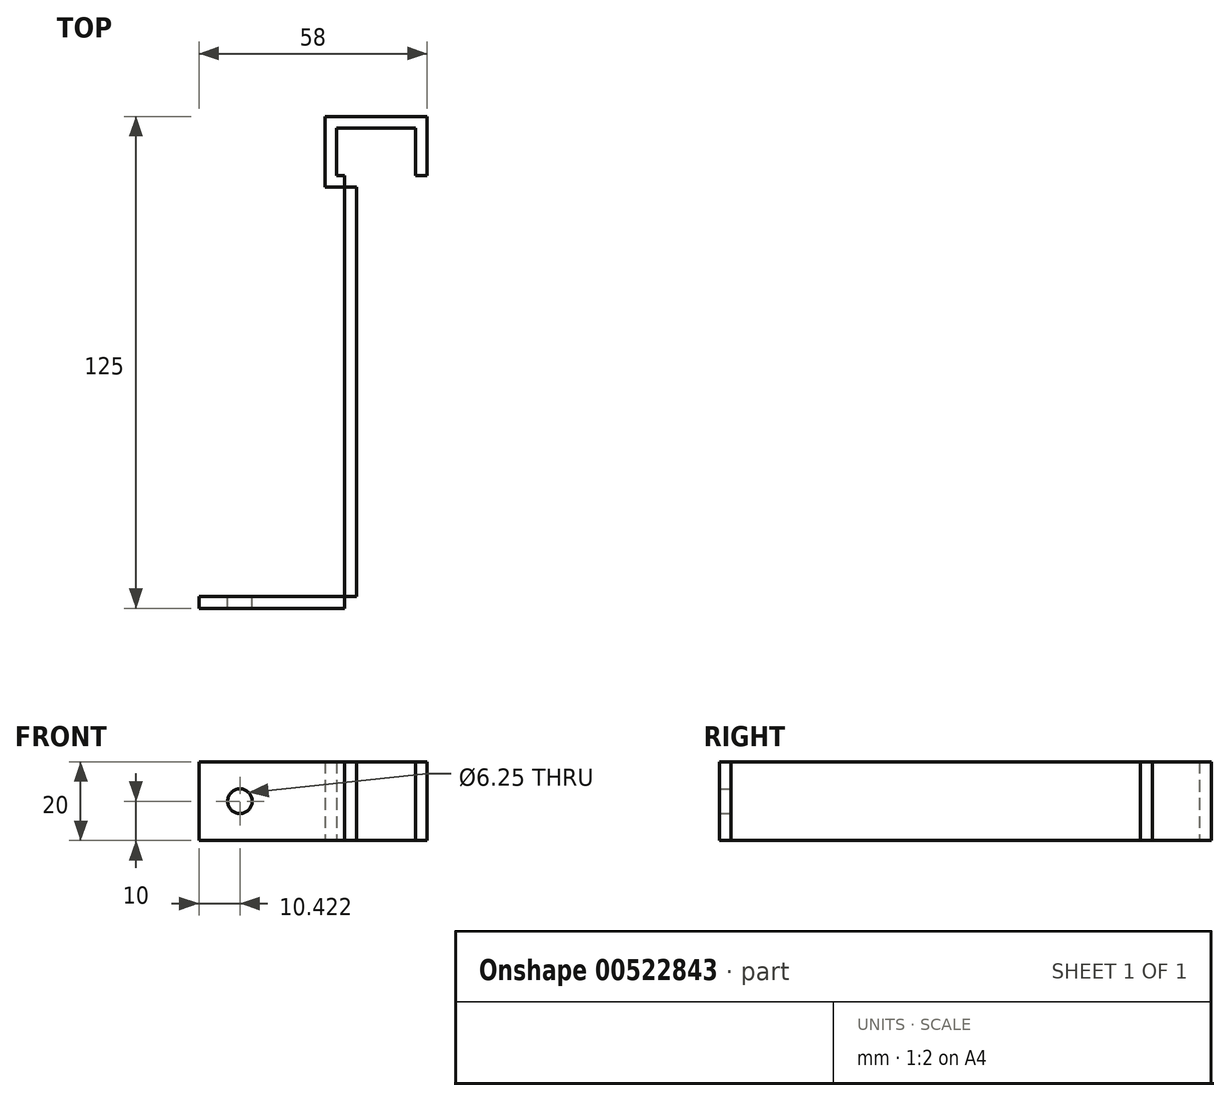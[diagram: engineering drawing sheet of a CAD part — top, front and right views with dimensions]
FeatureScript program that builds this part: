
annotation { "Feature Type Name" : "Feature", "Feature Type Description" : "" }
export const myFeature = defineFeature(function(context is Context, id is Id, definition is map)
    precondition{}
    {
        {
            var Q0;
            Q0=qCreatedBy(makeId("Top.planeOp"),FACE);
            var sketch = newSketch(context, id + "F0", { "sketchPlane" : qUnion([Q0])});
            skLineSegment(sketch, "E0.bottom", {"start": v(0, 38.47) * mm, "end": v(3, 38.47) * mm});
            skLineSegment(sketch, "E0.top", {"start": v(0, 23.47) * mm, "end": v(3, 23.47) * mm});
            skLineSegment(sketch, "E0.left", {"start": v(0, 38.47) * mm, "end": v(0, 23.47) * mm});
            skLineSegment(sketch, "E0.right", {"start": v(3, 38.47) * mm, "end": v(3, 23.47) * mm});
            skLineSegment(sketch, "E1.bottom", {"start": v(0, 38.47) * mm, "end": v(-23, 38.47) * mm});
            skLineSegment(sketch, "E1.top", {"start": v(0, 35.47) * mm, "end": v(-23, 35.47) * mm});
            skLineSegment(sketch, "E1.left", {"start": v(0, 38.47) * mm, "end": v(0, 35.47) * mm});
            skLineSegment(sketch, "E1.right", {"start": v(-23, 38.47) * mm, "end": v(-23, 35.47) * mm});
            skLineSegment(sketch, "E2.bottom", {"start": v(-23, 38.47) * mm, "end": v(-20, 38.47) * mm});
            skLineSegment(sketch, "E2.top", {"start": v(-23, 23.47) * mm, "end": v(-20, 23.47) * mm});
            skLineSegment(sketch, "E2.left", {"start": v(-23, 38.47) * mm, "end": v(-23, 23.47) * mm});
            skLineSegment(sketch, "E2.right", {"start": v(-20, 38.47) * mm, "end": v(-20, 23.47) * mm});
            skLineSegment(sketch, "E3.bottom", {"start": v(-23, 23.47) * mm, "end": v(-15, 23.47) * mm});
            skLineSegment(sketch, "E3.top", {"start": v(-23, 20.47) * mm, "end": v(-15, 20.47) * mm});
            skLineSegment(sketch, "E3.left", {"start": v(-23, 23.47) * mm, "end": v(-23, 20.47) * mm});
            skLineSegment(sketch, "E3.right", {"start": v(-15, 23.47) * mm, "end": v(-15, 20.47) * mm});
            skLineSegment(sketch, "E4.bottom", {"start": v(-15, 23.47) * mm, "end": v(-18, 23.47) * mm});
            skLineSegment(sketch, "E4.top", {"start": v(-15, -86.53) * mm, "end": v(-18, -86.53) * mm});
            skLineSegment(sketch, "E4.left", {"start": v(-15, 23.47) * mm, "end": v(-15, -86.53) * mm});
            skLineSegment(sketch, "E4.right", {"start": v(-18, 23.47) * mm, "end": v(-18, -86.53) * mm});
            skLineSegment(sketch, "E5.bottom", {"start": v(-15, -86.53) * mm, "end": v(-55, -86.53) * mm});
            skLineSegment(sketch, "E5.top", {"start": v(-15, -83.53) * mm, "end": v(-55, -83.53) * mm});
            skLineSegment(sketch, "E5.left", {"start": v(-15, -86.53) * mm, "end": v(-15, -83.53) * mm});
            skLineSegment(sketch, "E5.right", {"start": v(-55, -86.53) * mm, "end": v(-55, -83.53) * mm});
            skSolve(sketch);
        }
        {
            var Q0;
            Q0=makeQuery(id+"F0.imprint","IMPRINT",FACE,{"disambiguationData":[TD([[makeQuery(id+"F0.imprint","IMPRINT",EDGE,{"derivedFrom":sQuery(id+"F0.wireOp",EDGE,"E0.bottom")}),-1.0]])]});
            var Q1;
            {var subQ0=sQuery(id+"F0.wireOp",EDGE,"E1.bottom");Q1=makeQuery(id+"F0.imprint","IMPRINT",FACE,{"disambiguationData":[TD([[makeQuery(id+"F0.imprint","IMPRINT",EDGE,{"derivedFrom":subQ0}),1.0]])]});}
            var Q2;
            {var subQ5=sQuery(id+"F0.wireOp",EDGE,"E2.bottom");Q2=makeQuery(id+"F0.imprint","IMPRINT",FACE,{"disambiguationData":[TD([[makeQuery(id+"F0.imprint","IMPRINT",EDGE,{"derivedFrom":subQ5}),-1.0]])]});}
            var Q3;
            {var subQ0=sQuery(id+"F0.wireOp",EDGE,"E2.left");var subQ1=sQuery(id+"F0.wireOp",EDGE,"E1.top");var subQ2=makeQuery(id+"F0.imprint","INTERSECT",VERTEX,{"derivedFrom":[subQ1,subQ0]});Q3=makeQuery(id+"F0.imprint","IMPRINT",FACE,{"disambiguationData":[TD([[makeQuery(id+"F0.imprint","IMPRINT",EDGE,{"disambiguationData":[TD([[subQ2,1.0]])],"derivedFrom":subQ1}),1.0]])]});}
            var Q4;
            {var subQ0=sQuery(id+"F0.wireOp",EDGE,"E3.left");Q4=makeQuery(id+"F0.imprint","IMPRINT",FACE,{"disambiguationData":[TD([[makeQuery(id+"F0.imprint","IMPRINT",EDGE,{"derivedFrom":subQ0}),1.0]])]});}
            var Q5;
            {var subQ5=sQuery(id+"F0.wireOp",EDGE,"E4.bottom");Q5=makeQuery(id+"F0.imprint","IMPRINT",FACE,{"disambiguationData":[TD([[makeQuery(id+"F0.imprint","IMPRINT",EDGE,{"derivedFrom":subQ5}),1.0]])]});}
            var Q6;
            {var subQ0=sQuery(id+"F0.wireOp",EDGE,"E4.left");var subQ1=sQuery(id+"F0.wireOp",EDGE,"E3.top");var subQ2=makeQuery(id+"F0.imprint","INTERSECT",VERTEX,{"derivedFrom":[subQ1,subQ0]});Q6=makeQuery(id+"F0.imprint","IMPRINT",FACE,{"disambiguationData":[TD([[makeQuery(id+"F0.imprint","IMPRINT",EDGE,{"disambiguationData":[TD([[subQ2,1.0]])],"derivedFrom":subQ1}),-1.0]])]});}
            var Q7;
            {var subQ5=sQuery(id+"F0.wireOp",EDGE,"E5.left");Q7=makeQuery(id+"F0.imprint","IMPRINT",FACE,{"disambiguationData":[TD([[makeQuery(id+"F0.imprint","IMPRINT",EDGE,{"derivedFrom":subQ5}),1.0]])]});}
            var Q8;
            {var subQ5=sQuery(id+"F0.wireOp",EDGE,"E5.right");Q8=makeQuery(id+"F0.imprint","IMPRINT",FACE,{"disambiguationData":[TD([[makeQuery(id+"F0.imprint","IMPRINT",EDGE,{"derivedFrom":subQ5}),-1.0]])]});}
            extrude(context, id + "F1", {"entities" : qUnion([Q0, Q1, Q2, Q3, Q4, Q5, Q6, Q7, Q8]), "depth" : 20 * mm, "offsetDistance" : 25 * mm});
        }
        {
            var Q0;
            Q0=makeQuery(id+"F1.opExtrude","SWEPT_FACE",FACE,{"disambiguationData":[OSD([sQuery(id+"F0.wireOp",EDGE,"E5.top")])]});
            var sketch = newSketch(context, id + "F2", { "sketchPlane" : qUnion([Q0])});
            skCircle(sketch, "E6", {"center": v(44.58, 10) * mm, "radius": 3.12 * mm});
            skSolve(sketch);
        }
        {
            var Q0;
            Q0=makeQuery(id+"F2.imprint","IMPRINT",FACE,{"disambiguationData":[TD([[makeQuery(id+"F2.imprint","IMPRINT",EDGE,{"derivedFrom":sQuery(id+"F2.wireOp",EDGE,"E6")}),1.0]])]});
            extrude(context, id + "F3", {"entities" : qUnion([Q0]), "operationType" : NewBodyOperationType.REMOVE, "endBound" : BoundingType.THROUGH_ALL, "oppositeDirection" : true, "depth" : 25 * mm, "offsetDistance" : 25 * mm});
        }
    });
